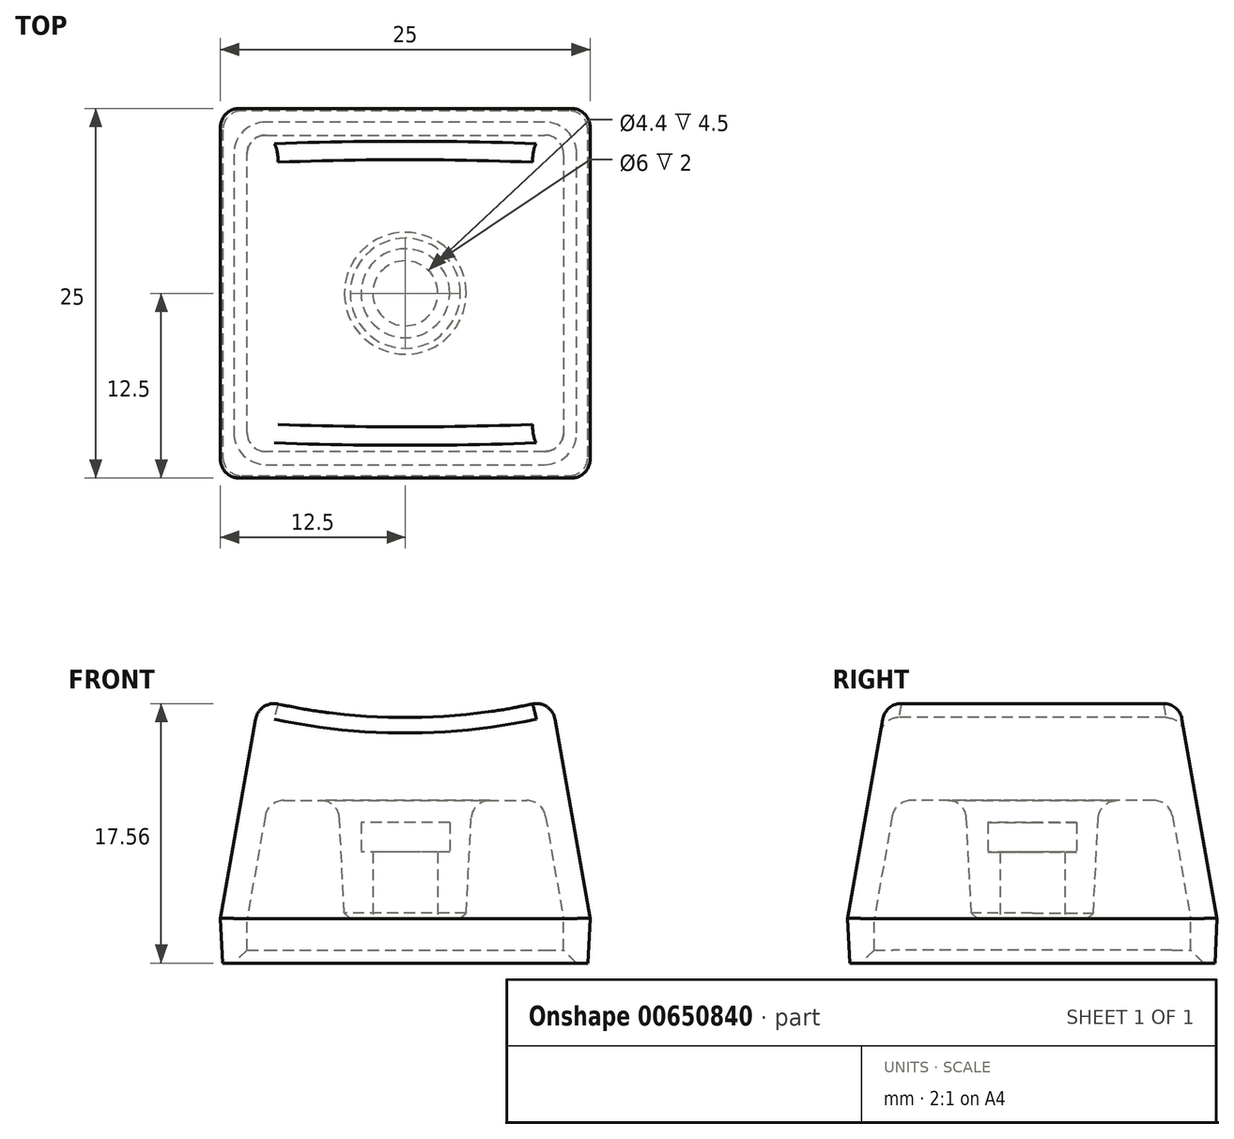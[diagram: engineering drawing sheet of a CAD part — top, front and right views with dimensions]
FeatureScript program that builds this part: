
annotation { "Feature Type Name" : "Feature", "Feature Type Description" : "" }
export const myFeature = defineFeature(function(context is Context, id is Id, definition is map)
    precondition{}
    {
        {
            var Q0;
            Q0=qCreatedBy(makeId("Top.planeOp"),FACE);
            var sketch = newSketch(context, id + "F0", { "sketchPlane" : qUnion([Q0])});
            skLineSegment(sketch, "E0.bottom", {"start": v(12.5, 12.5) * mm, "end": v(-12.5, 12.5) * mm});
            skLineSegment(sketch, "E0.top", {"start": v(12.5, -12.5) * mm, "end": v(-12.5, -12.5) * mm});
            skLineSegment(sketch, "E0.left", {"start": v(12.5, 12.5) * mm, "end": v(12.5, -12.5) * mm});
            skLineSegment(sketch, "E0.right", {"start": v(-12.5, 12.5) * mm, "end": v(-12.5, -12.5) * mm});
            skPoint(sketch, "E0.middle", {"position": v(0, 0) * mm});
            skPoint(sketch, "E1.right.end.orphan", {"position": v(-19.05, 19.05) * mm});
            skPoint(sketch, "E1.bottom.end.orphan", {"position": v(-19.05, -19.05) * mm});
            skPoint(sketch, "E1.left.end.orphan", {"position": v(19.05, 19.05) * mm});
            skPoint(sketch, "E1.left.start.orphan", {"position": v(19.05, -19.05) * mm});
            skSolve(sketch);
        }
        {
            var Q0;
            Q0=qSketchRegion(id+"F0",true);
            extrude(context, id + "F1", {"entities" : qUnion([Q0]), "depth" : 15 * mm, "offsetDistance" : 25.4 * mm, "hasDraft" : true, "draftAngle" : 10 * degree, "draftPullDirection" : true});
        }
        {
            var Q0;
            Q0=qCreatedBy(makeId("Top.planeOp"),FACE);
            var sketch = newSketch(context, id + "F2", { "sketchPlane" : qUnion([Q0])});
            skLineSegment(sketch, "E2.bottom", {"start": v(10.7, 10.7) * mm, "end": v(-10.7, 10.7) * mm});
            skLineSegment(sketch, "E2.top", {"start": v(10.7, -10.7) * mm, "end": v(-10.7, -10.7) * mm});
            skLineSegment(sketch, "E2.left", {"start": v(10.7, 10.7) * mm, "end": v(10.7, -10.7) * mm});
            skLineSegment(sketch, "E2.right", {"start": v(-10.7, 10.7) * mm, "end": v(-10.7, -10.7) * mm});
            skPoint(sketch, "E2.middle", {"position": v(0, 0) * mm});
            skSolve(sketch);
        }
        {
            var Q0;
            Q0=qSketchRegion(id+"F2",true);
            extrude(context, id + "F3", {"entities" : qUnion([Q0]), "operationType" : NewBodyOperationType.REMOVE, "depth" : 8 * mm, "offsetDistance" : 25.4 * mm, "hasDraft" : true, "draftAngle" : 10 * degree, "draftPullDirection" : true});
        }
        {
            var Q0;
            Q0=makeQuery(id+"F3.boolean.opBoolean","COPY",EDGE,{"derivedFrom":makeQuery(id+"F3.opExtrude","CAP_EDGE",EDGE,{"disambiguationData":[OSD([sQuery(id+"F2.wireOp",EDGE,"E2.bottom")])],"isStart":false})});
            var Q1;
            Q1=makeQuery(id+"F3.boolean.opBoolean","COPY",EDGE,{"derivedFrom":makeQuery(id+"F3.opExtrude","CAP_EDGE",EDGE,{"disambiguationData":[OSD([sQuery(id+"F2.wireOp",EDGE,"E2.right")])],"isStart":false})});
            var Q2;
            Q2=makeQuery(id+"F3.boolean.opBoolean","COPY",EDGE,{"derivedFrom":makeQuery(id+"F3.opExtrude","CAP_EDGE",EDGE,{"disambiguationData":[OSD([sQuery(id+"F2.wireOp",EDGE,"E2.top")])],"isStart":false})});
            var Q3;
            Q3=makeQuery(id+"F3.boolean.opBoolean","COPY",EDGE,{"derivedFrom":makeQuery(id+"F3.opExtrude","CAP_EDGE",EDGE,{"disambiguationData":[OSD([sQuery(id+"F2.wireOp",EDGE,"E2.left")])],"isStart":false})});
            fillet(context, id + "F4", {"entities" : qUnion([Q0, Q1, Q2, Q3]), "radius" : 1.27 * mm, "tangentPropagation" : true, "allowEdgeOverflow" : false});
        }
        {
            var Q0;
            Q0=makeQuery(id+"F4.opFillet","BLEND_EDGE",EDGE,{"blendedFrom":[makeQuery(id+"F3.boolean.opBoolean","COPY",EDGE,{"derivedFrom":makeQuery(id+"F3.opExtrude","CAP_EDGE",EDGE,{"disambiguationData":[OSD([sQuery(id+"F2.wireOp",EDGE,"E2.bottom")])],"isStart":false})}),makeQuery(id+"F3.boolean.opBoolean","COPY",EDGE,{"derivedFrom":makeQuery(id+"F3.opExtrude","CAP_EDGE",EDGE,{"disambiguationData":[OSD([sQuery(id+"F2.wireOp",EDGE,"E2.right")])],"isStart":false})})],"blendedInto":[]});
            var Q1;
            Q1=makeQuery(id+"F4.opFillet","BLEND_EDGE",EDGE,{"blendedFrom":[makeQuery(id+"F3.boolean.opBoolean","COPY",EDGE,{"derivedFrom":makeQuery(id+"F3.opExtrude","CAP_EDGE",EDGE,{"disambiguationData":[OSD([sQuery(id+"F2.wireOp",EDGE,"E2.bottom")])],"isStart":false})}),makeQuery(id+"F3.boolean.opBoolean","COPY",EDGE,{"derivedFrom":makeQuery(id+"F3.opExtrude","CAP_EDGE",EDGE,{"disambiguationData":[OSD([sQuery(id+"F2.wireOp",EDGE,"E2.left")])],"isStart":false})})],"blendedInto":[]});
            var Q2;
            Q2=makeQuery(id+"F4.opFillet","BLEND_EDGE",EDGE,{"blendedFrom":[makeQuery(id+"F3.boolean.opBoolean","COPY",EDGE,{"derivedFrom":makeQuery(id+"F3.opExtrude","CAP_EDGE",EDGE,{"disambiguationData":[OSD([sQuery(id+"F2.wireOp",EDGE,"E2.top")])],"isStart":false})}),makeQuery(id+"F3.boolean.opBoolean","COPY",EDGE,{"derivedFrom":makeQuery(id+"F3.opExtrude","CAP_EDGE",EDGE,{"disambiguationData":[OSD([sQuery(id+"F2.wireOp",EDGE,"E2.left")])],"isStart":false})})],"blendedInto":[]});
            var Q3;
            Q3=makeQuery(id+"F4.opFillet","BLEND_EDGE",EDGE,{"blendedFrom":[makeQuery(id+"F3.boolean.opBoolean","COPY",EDGE,{"derivedFrom":makeQuery(id+"F3.opExtrude","CAP_EDGE",EDGE,{"disambiguationData":[OSD([sQuery(id+"F2.wireOp",EDGE,"E2.top")])],"isStart":false})}),makeQuery(id+"F3.boolean.opBoolean","COPY",EDGE,{"derivedFrom":makeQuery(id+"F3.opExtrude","CAP_EDGE",EDGE,{"disambiguationData":[OSD([sQuery(id+"F2.wireOp",EDGE,"E2.right")])],"isStart":false})})],"blendedInto":[]});
            fillet(context, id + "F5", {"entities" : qUnion([Q0, Q1, Q2, Q3]), "radius" : 1.27 * mm, "tangentPropagation" : true, "allowEdgeOverflow" : false});
        }
        {
            var Q0;
            Q0=makeQuery(id+"F0.imprint","IMPRINT",FACE,{"disambiguationData":[TD([[makeQuery(id+"F0.imprint","IMPRINT",EDGE,{"derivedFrom":sQuery(id+"F0.wireOp",EDGE,"E0.bottom")}),1.0]])]});
            extrude(context, id + "F6", {"entities" : qUnion([Q0]), "operationType" : NewBodyOperationType.ADD, "oppositeDirection" : true, "depth" : 3 * mm, "offsetDistance" : 25.4 * mm, "hasDraft" : true, "draftAngle" : 3 * degree, "draftPullDirection" : true});
        }
        {
            var Q0;
            Q0=makeQuery(id+"F2.imprint","IMPRINT",FACE,{"disambiguationData":[TD([[makeQuery(id+"F2.imprint","IMPRINT",EDGE,{"derivedFrom":sQuery(id+"F2.wireOp",EDGE,"E2.bottom")}),1.0]])]});
            extrude(context, id + "F7", {"entities" : qUnion([Q0]), "operationType" : NewBodyOperationType.REMOVE, "oppositeDirection" : true, "depth" : 25.4 * mm, "offsetDistance" : 25.4 * mm});
        }
        {
            var Q0;
            Q0=makeQuery(id+"F7.boolean.opBoolean","COPY",EDGE,{"derivedFrom":makeQuery(id+"F7.opExtrude","SWEPT_EDGE",EDGE,{"disambiguationData":[OSD([sQuery(id+"F2.wireOp",EDGE,"E2.bottom"),sQuery(id+"F2.wireOp",EDGE,"E2.right")])]})});
            var Q1;
            Q1=makeQuery(id+"F7.boolean.opBoolean","COPY",EDGE,{"derivedFrom":makeQuery(id+"F7.opExtrude","SWEPT_EDGE",EDGE,{"disambiguationData":[OSD([sQuery(id+"F2.wireOp",EDGE,"E2.top"),sQuery(id+"F2.wireOp",EDGE,"E2.right")])]})});
            var Q2;
            Q2=makeQuery(id+"F7.boolean.opBoolean","COPY",EDGE,{"derivedFrom":makeQuery(id+"F7.opExtrude","SWEPT_EDGE",EDGE,{"disambiguationData":[OSD([sQuery(id+"F2.wireOp",EDGE,"E2.bottom"),sQuery(id+"F2.wireOp",EDGE,"E2.left")])]})});
            var Q3;
            Q3=makeQuery(id+"F7.boolean.opBoolean","COPY",EDGE,{"derivedFrom":makeQuery(id+"F7.opExtrude","SWEPT_EDGE",EDGE,{"disambiguationData":[OSD([sQuery(id+"F2.wireOp",EDGE,"E2.top"),sQuery(id+"F2.wireOp",EDGE,"E2.left")])]})});
            fillet(context, id + "F8", {"entities" : qUnion([Q0, Q1, Q2, Q3]), "radius" : 1.27 * mm, "tangentPropagation" : true, "allowEdgeOverflow" : false});
        }
        {
            var Q0;
            Q0=makeQuery(id+"F6.opExtrude","SWEPT_EDGE",EDGE,{"disambiguationData":[OSD([sQuery(id+"F0.wireOp",EDGE,"E0.bottom"),sQuery(id+"F0.wireOp",EDGE,"E0.right")])]});
            var Q1;
            Q1=makeQuery(id+"F6.opExtrude","SWEPT_EDGE",EDGE,{"disambiguationData":[OSD([sQuery(id+"F0.wireOp",EDGE,"E0.bottom"),sQuery(id+"F0.wireOp",EDGE,"E0.left")])]});
            var Q2;
            Q2=makeQuery(id+"F6.opExtrude","SWEPT_EDGE",EDGE,{"disambiguationData":[OSD([sQuery(id+"F0.wireOp",EDGE,"E0.top"),sQuery(id+"F0.wireOp",EDGE,"E0.right")])]});
            var Q3;
            Q3=makeQuery(id+"F6.opExtrude","SWEPT_EDGE",EDGE,{"disambiguationData":[OSD([sQuery(id+"F0.wireOp",EDGE,"E0.top"),sQuery(id+"F0.wireOp",EDGE,"E0.left")])]});
            fillet(context, id + "F9", {"entities" : qUnion([Q0, Q1, Q2, Q3]), "radius" : 1.27 * mm, "tangentPropagation" : true, "allowEdgeOverflow" : false});
        }
        {
            var Q0;
            Q0=qCreatedBy(makeId("Front.planeOp"),FACE);
            var sketch = newSketch(context, id + "F10", { "sketchPlane" : qUnion([Q0])});
            skLineSegment(sketch, "E3", {"start": v(0, 0) * mm, "end": v(0, 51.98) * mm});
            skEllipse(sketch, "E4", {"center": v(0, 28.61) * mm, "majorRadius": 25 * mm, "minorRadius": 15 * mm, "majorAxis": v(1, 0)});
            skSolve(sketch);
        }
        {
            var Q0;
            Q0=qSketchRegion(id+"F10",true);
            extrude(context, id + "F11", {"entities" : qUnion([Q0]), "operationType" : NewBodyOperationType.REMOVE, "depth" : 34.3 * mm, "offsetDistance" : 25.4 * mm, "hasSecondDirection" : true, "secondDirectionOppositeDirection" : true, "secondDirectionDepth" : 34.3 * mm});
        }
        {
            var Q0;
            Q0=makeQuery(id+"F11.boolean.opBoolean","INTERSECT",EDGE,{"derivedFrom":[makeQuery(id+"F1.opExtrude","SWEPT_FACE",FACE,{"disambiguationData":[OSD([sQuery(id+"F0.wireOp",EDGE,"E0.top")])]}),makeQuery(id+"F11.opExtrude","SWEPT_FACE",FACE,{"disambiguationData":[OSD([sQuery(id+"F10.wireOp",EDGE,"E4")])]})]});
            var Q1;
            Q1=makeQuery(id+"F1.opExtrude","SWEPT_EDGE",EDGE,{"disambiguationData":[OSD([sQuery(id+"F0.wireOp",EDGE,"E0.top"),sQuery(id+"F0.wireOp",EDGE,"E0.right")])]});
            var Q2;
            Q2=makeQuery(id+"F11.boolean.opBoolean","INTERSECT",EDGE,{"derivedFrom":[makeQuery(id+"F1.opExtrude","SWEPT_FACE",FACE,{"disambiguationData":[OSD([sQuery(id+"F0.wireOp",EDGE,"E0.right")])]}),makeQuery(id+"F11.opExtrude","SWEPT_FACE",FACE,{"disambiguationData":[OSD([sQuery(id+"F10.wireOp",EDGE,"E4")])]})]});
            var Q3;
            Q3=makeQuery(id+"F1.opExtrude","SWEPT_EDGE",EDGE,{"disambiguationData":[OSD([sQuery(id+"F0.wireOp",EDGE,"E0.top"),sQuery(id+"F0.wireOp",EDGE,"E0.left")])]});
            var Q4;
            Q4=makeQuery(id+"F11.boolean.opBoolean","INTERSECT",EDGE,{"derivedFrom":[makeQuery(id+"F1.opExtrude","SWEPT_FACE",FACE,{"disambiguationData":[OSD([sQuery(id+"F0.wireOp",EDGE,"E0.left")])]}),makeQuery(id+"F11.opExtrude","SWEPT_FACE",FACE,{"disambiguationData":[OSD([sQuery(id+"F10.wireOp",EDGE,"E4")])]})]});
            var Q5;
            Q5=makeQuery(id+"F1.opExtrude","SWEPT_EDGE",EDGE,{"disambiguationData":[OSD([sQuery(id+"F0.wireOp",EDGE,"E0.bottom"),sQuery(id+"F0.wireOp",EDGE,"E0.left")])]});
            var Q6;
            Q6=makeQuery(id+"F11.boolean.opBoolean","INTERSECT",EDGE,{"derivedFrom":[makeQuery(id+"F1.opExtrude","SWEPT_FACE",FACE,{"disambiguationData":[OSD([sQuery(id+"F0.wireOp",EDGE,"E0.bottom")])]}),makeQuery(id+"F11.opExtrude","SWEPT_FACE",FACE,{"disambiguationData":[OSD([sQuery(id+"F10.wireOp",EDGE,"E4")])]})]});
            var Q7;
            Q7=makeQuery(id+"F1.opExtrude","SWEPT_EDGE",EDGE,{"disambiguationData":[OSD([sQuery(id+"F0.wireOp",EDGE,"E0.bottom"),sQuery(id+"F0.wireOp",EDGE,"E0.right")])]});
            fillet(context, id + "F12", {"entities" : qUnion([Q0, Q1, Q2, Q3, Q4, Q5, Q6, Q7]), "radius" : 1.27 * mm, "tangentPropagation" : true, "allowEdgeOverflow" : false});
        }
        {
            var Q0;
            Q0=qCreatedBy(makeId("Top.planeOp"),FACE);
            var sketch = newSketch(context, id + "F13", { "sketchPlane" : qUnion([Q0])});
            skCircle(sketch, "E5", {"center": v(0, 0) * mm, "radius": 4.1 * mm});
            skSolve(sketch);
        }
        {
            var Q0;
            Q0=qSketchRegion(id+"F13",true);
            extrude(context, id + "F14", {"entities" : qUnion([Q0]), "operationType" : NewBodyOperationType.ADD, "depth" : 8.9 * mm, "offsetDistance" : 25.4 * mm, "hasDraft" : true, "draftAngle" : 3 * degree, "hasSecondDirectionDraft" : true, "secondDirectionDraftAngle" : 3 * degree, "secondDirectionDraftPullDirection" : true});
        }
        {
            var Q0;
            Q0=makeQuery(id+"F14.boolean.opBoolean","INTERSECT",EDGE,{"derivedFrom":[makeQuery(id+"F3.boolean.opBoolean","COPY",FACE,{"derivedFrom":makeQuery(id+"F3.opExtrude","CAP_FACE",FACE,{"disambiguationData":[OSD([sQuery(id+"F2.wireOp",EDGE,"E2.bottom"),sQuery(id+"F2.wireOp",EDGE,"E2.top"),sQuery(id+"F2.wireOp",EDGE,"E2.left"),sQuery(id+"F2.wireOp",EDGE,"E2.right")])],"isStart":false})}),makeQuery(id+"F14.opExtrude","SWEPT_FACE",FACE,{"disambiguationData":[OSD([sQuery(id+"F13.wireOp",EDGE,"E5")])]})]});
            fillet(context, id + "F15", {"entities" : qUnion([Q0]), "radius" : 1.27 * mm, "tangentPropagation" : true, "allowEdgeOverflow" : false});
        }
        {
            var Q0;
            Q0=makeQuery(id+"F7.boolean.opBoolean","INTERSECT",EDGE,{"derivedFrom":[makeQuery(id+"F6.opExtrude","CAP_FACE",FACE,{"disambiguationData":[OSD([sQuery(id+"F0.wireOp",EDGE,"E0.bottom"),sQuery(id+"F0.wireOp",EDGE,"E0.top"),sQuery(id+"F0.wireOp",EDGE,"E0.left"),sQuery(id+"F0.wireOp",EDGE,"E0.right")])],"isStart":false}),makeQuery(id+"F7.opExtrude","SWEPT_FACE",FACE,{"disambiguationData":[OSD([sQuery(id+"F2.wireOp",EDGE,"E2.top")])]})]});
            chamfer(context, id + "F16", {"entities" : qUnion([Q0]), "width" : .889 * mm, "tangentPropagation" : true});
        }
        {
            var Q0;
            Q0=qCreatedBy(makeId("Top.planeOp"),FACE);
            cPlane(context, id + "F17", {"entities" : qUnion([Q0]), "cplaneType" : CPlaneType.OFFSET, "offset" : 0 * mm, "oppositeDirection" : true, "width" : 150 * mm, "height" : 150 * mm});
        }
        {
            var Q0;
            Q0=qCreatedBy(id+"F17.planeOp",FACE);
            var sketch = newSketch(context, id + "F18", { "sketchPlane" : qUnion([Q0])});
            skCircle(sketch, "E6", {"center": v(0, 0) * mm, "radius": 2.2 * mm});
            skSolve(sketch);
        }
        {
            var Q0;
            Q0 = qSketchRegion(id + "F18", true);
            extrude(context, id + "F19", {"entities" : qUnion([Q0]), "operationType" : NewBodyOperationType.REMOVE, "depth" : 4.5 * mm, "offsetDistance" : 25 * mm});
        }
        {
            var Q0;
            Q0=qCreatedBy(id+"F17.planeOp",FACE);
            cPlane(context, id + "F20", {"entities" : qUnion([Q0]), "cplaneType" : CPlaneType.OFFSET, "offset" : 4.5 * mm, "width" : 150 * mm, "height" : 150 * mm});
        }
        {
            var Q0;
            Q0=qCreatedBy(id+"F20.planeOp",FACE);
            var sketch = newSketch(context, id + "F21", { "sketchPlane" : qUnion([Q0])});
            skCircle(sketch, "E7", {"center": v(0, 0) * mm, "radius": 3 * mm});
            skSolve(sketch);
        }
        {
            var Q0;
            Q0 = qSketchRegion(id + "F21", true);
            extrude(context, id + "F22", {"entities" : qUnion([Q0]), "operationType" : NewBodyOperationType.REMOVE, "depth" : 2 * mm, "offsetDistance" : 25 * mm});
        }
        {
            var Q0;
            Q0=makeQuery(id+"F14.opExtrude","CAP_EDGE",EDGE,{"disambiguationData":[OSD([sQuery(id+"F13.wireOp",EDGE,"E5")])],"isStart":true});
            chamfer(context, id + "F23", {"entities" : qUnion([Q0]), "width" : .4 * mm, "tangentPropagation" : true});
        }
    });
